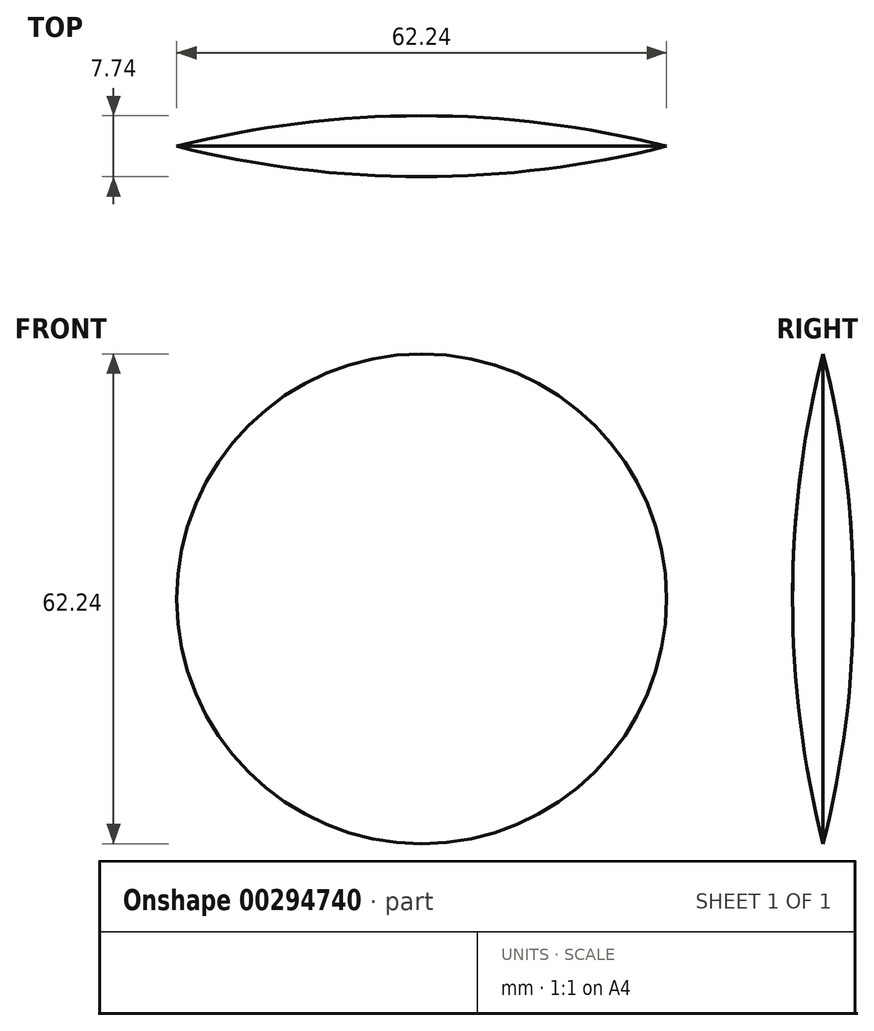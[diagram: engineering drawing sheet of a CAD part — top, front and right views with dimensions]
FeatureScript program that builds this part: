
annotation { "Feature Type Name" : "Feature", "Feature Type Description" : "" }
export const myFeature = defineFeature(function(context is Context, id is Id, definition is map)
    precondition{}
    {
        {
            var Q0;
            Q0=qCreatedBy(makeId("Right.planeOp"),FACE);
            var sketch = newSketch(context, id + "F0", { "sketchPlane" : qUnion([Q0])});
            skArc(sketch, "E0", {"start": v(0, 31.12) * mm, "mid": v(-2.9, 15.68) * mm, "end": v(-3.87, 0) * mm});
            skArc(sketch, "E1", {"start": v(3.87, 0) * mm, "mid": v(2.9, 15.68) * mm, "end": v(0, 31.12) * mm});
            skLineSegment(sketch, "E2", {"start": v(0, 0) * mm, "end": v(-3.87, 0) * mm});
            skLineSegment(sketch, "E3", {"start": v(0, 0) * mm, "end": v(3.87, 0) * mm});
            skSolve(sketch);
        }
        {
            var Q0;
            Q0=qSketchRegion(id+"F0",true);
            var Q1;
            Q1=sQuery(id+"F0.wireOp",EDGE,"E3");
            revolve(context, id + "F1", {"entities" : qUnion([Q0]), "axis" : qUnion([Q1]), "revolveType" : RevolveType.FULL});
        }
    });
